# Revit family: 63_UN_Floodlight_SWL-A 17000LM_Norton
name_source: partatom
category: Lighting Fixtures
units: mm (PartAtom-declared; Revit-internal decimal feet)

## family parameters
Always vertical = Yes
Cut with Voids When Loaded = Yes
Light Source = No
OmniClass Number = 23.80.70.11.14.11
OmniClass Title = Downlights
Part Type = Normal
Room Calculation Point = Yes
Round Connector Dimension = Use Diameter
Shared = No
Work Plane-Based = No

## types (1)
- SWL-A 84 17000LM
    Apparent Load = 150 VA
    Assembly Code = 63.0
    Height = 67 mm  [stored 0.219816 ft]
    Housing_Material = Black
    IfcExportAs = IfcLightFixtureType
    IfcExportType = USERDEFINED
    Lamp = LED
    Length = 485 mm  [stored 1.59121 ft]
    Light Source = Geometry
    Luminous Flux (lm) = 20150 lm
    Manufacturer = Norton
    Model = SWL-A
    Type Comments = 17000LM
    URL = https://www.norton.nl
    Voltage = 230 V
    Wattage Comments = 150W
    Width = 354 mm  [stored 1.16142 ft]

note: [stored X ft] marks values corroborated as IEEE doubles in the binary element streams (Revit-internal decimal feet)

## geometry (parser evidence)
native form markers: Sweep x18
no freeform markers — native parametric forms only
